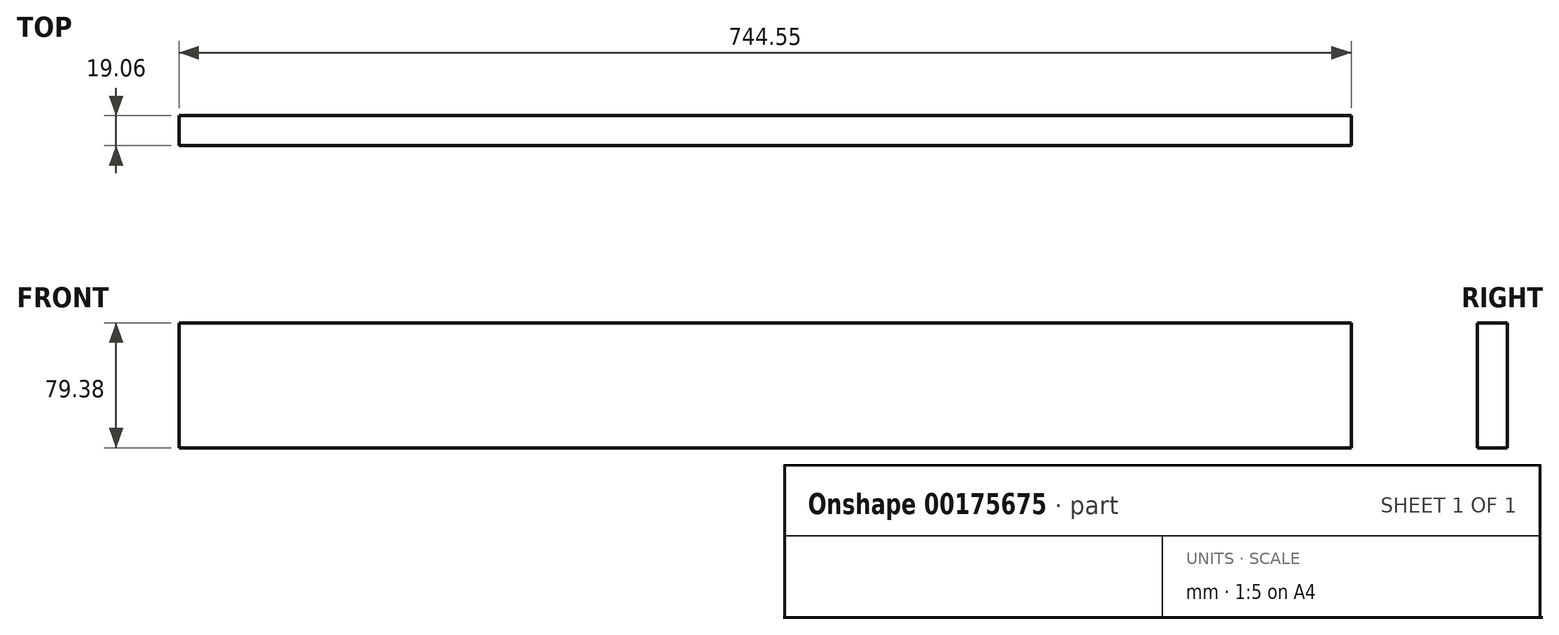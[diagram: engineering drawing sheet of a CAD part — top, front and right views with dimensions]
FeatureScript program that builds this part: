
annotation { "Feature Type Name" : "Feature", "Feature Type Description" : "" }
export const myFeature = defineFeature(function(context is Context, id is Id, definition is map)
    precondition{}
    {
        {
            var Q0;
            Q0=qCreatedBy(makeId("Right.planeOp"),FACE);
            var sketch = newSketch(context, id + "F0", { "sketchPlane" : qUnion([Q0])});
            skLineSegment(sketch, "E0.bottom", {"start": v(9.52, -39.69) * mm, "end": v(-9.53, -39.69) * mm});
            skLineSegment(sketch, "E0.top", {"start": v(9.53, 39.69) * mm, "end": v(-9.52, 39.69) * mm});
            skLineSegment(sketch, "E0.left", {"start": v(9.52, -39.69) * mm, "end": v(9.53, 39.69) * mm});
            skLineSegment(sketch, "E0.right", {"start": v(-9.53, -39.69) * mm, "end": v(-9.52, 39.69) * mm});
            skPoint(sketch, "E0.middle", {"position": v(0, 0) * mm});
            skSolve(sketch);
        }
        {
            var Q0;
            Q0=makeQuery(id+"F0.imprint","IMPRINT",FACE,{"disambiguationData":[TD([[makeQuery(id+"F0.imprint","IMPRINT",EDGE,{"derivedFrom":sQuery(id+"F0.wireOp",EDGE,"E0.bottom")}),-1.0]])]});
            extrude(context, id + "F1", {"entities" : qUnion([Q0]), "depth" : 744.55 * mm});
        }
        {
            var Q0;
            Q0=makeQuery(id+"F1.opExtrude","SWEPT_FACE",FACE,{"disambiguationData":[OSD([sQuery(id+"F0.wireOp",EDGE,"E0.right")])]});
            var sketch = newSketch(context, id + "F2", { "sketchPlane" : qUnion([Q0])});
            skPoint(sketch, "E1", {"position": v(61.24, -26.99) * mm});
            skPoint(sketch, "E2", {"position": v(683.31, -26.99) * mm});
            skCircle(sketch, "E3", {"center": v(683.31, -26.99) * mm, "radius": 3.18 * mm});
            skCircle(sketch, "E4", {"center": v(61.24, -26.99) * mm, "radius": 3.18 * mm});
            skSolve(sketch);
        }
    });
